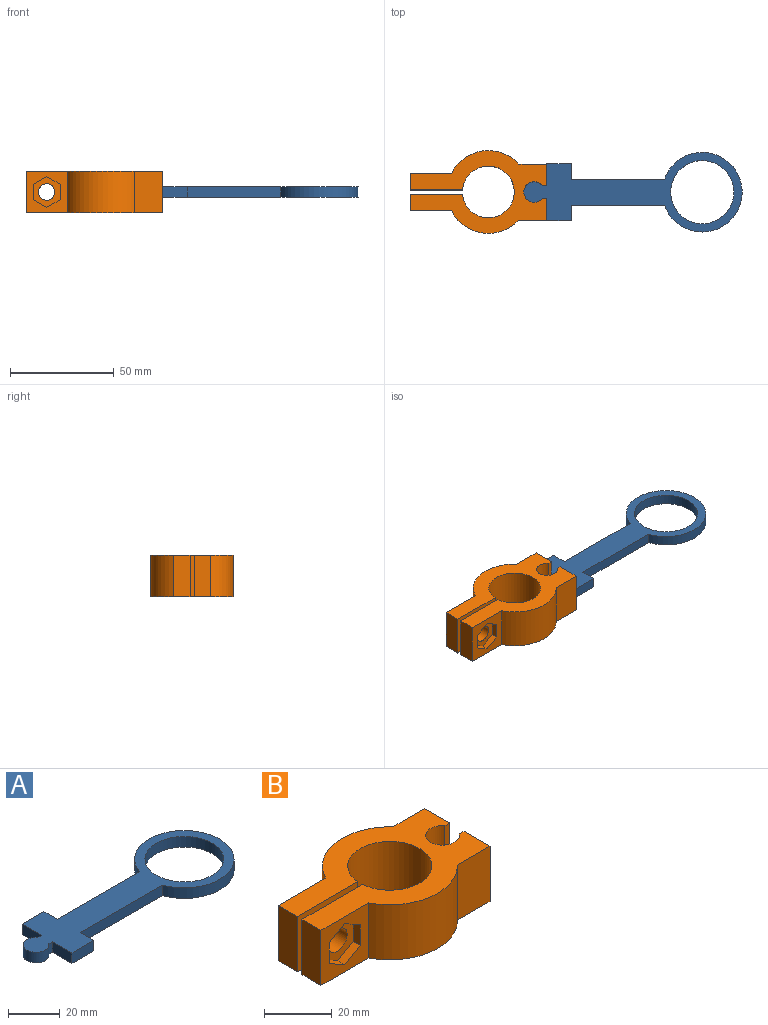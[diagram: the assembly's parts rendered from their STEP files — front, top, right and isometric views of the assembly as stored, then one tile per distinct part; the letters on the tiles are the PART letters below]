
ASSEMBLY  parts=2 mates=1
PART A: 15 faces, bbox 105.4x38.5x5 mm
  f0: plane 12x5mm, normal (0,-1,0), area 60mm2, adj f1,f12,f13,f14
  f1: plane 7.39x5mm, normal (1,0,0), area 37mm2, adj f0,f2,f13,f14
  f2: plane 44.99x5mm, normal (0,-1,0), area 224.9mm2, adj f1,f3,f13,f14
  f3: cylinder r=19.25mm len=38.5mm, axis (0,0,-1), area 540.7mm2, adj f2,f4,f13,f14
  f4: plane 44.99x5mm, normal (0,1,0), area 224.9mm2, adj f3,f5,f13,f14
  f5: plane 7.39x5mm, normal (1,0,0), area 37mm2, adj f4,f6,f13,f14
  f6: plane 12x5mm, normal (0,1,0), area 60mm2, adj f5,f7,f13,f14
  f7: plane 10.68x5mm, normal (-1,0,0), area 53.4mm2, adj f6,f8,f13,f14
  f8: plane 5x2mm, normal (0,1,0), area 10mm2, adj f7,f9,f13,f14
  f9: cylinder r=5mm len=10mm, axis (0,0,-1), area 124.9mm2, adj f8,f10,f13,f14
  f10: plane 5x2mm, normal (0,-1,0), area 10mm2, adj f9,f12,f13,f14
  f11: cylinder r=15.25mm len=30.5mm, axis (0,0,-1), area 479.1mm2, adj f13,f14
  f12: plane 10.68x5mm, normal (-1,0,0), area 53.4mm2, adj f0,f10,f13,f14
  f13: plane 105.43x38.5mm, normal (0,0,1), area 1405mm2, adj f0,f1,f2,f3,f4,f5,f6,f7
  f14: plane 105.43x38.5mm, normal (0,0,-1), area 1405mm2, adj f0,f1,f2,f3,f4,f5,f6,f7
PART B: 27 faces, bbox 66x40x20 mm
  f0: plane 20x20mm, normal (0,-1,0), area 253.6mm2, adj f4,f5,f16,f17,f18,f19,f20,f21
  f1: plane 25.4x20mm, normal (0,-1,0), area 457.8mm2, adj f2,f15,f16,f17,f26
  f2: cylinder r=12.5mm len=25mm, axis (0,0,-1), area 1530.8mm2, adj f1,f3,f16,f17
  f3: plane 25.41x20mm, normal (0,1,0), area 457.9mm2, adj f2,f4,f16,f17,f25
  f4: plane 20x7.96mm, normal (-1,0,0), area 159.2mm2, adj f0,f3,f16,f17
  f5: cylinder r=20mm len=32.28mm, axis (0,0,-1), area 763.8mm2, adj f0,f6,f16,f17
  f6: plane 20x13.7mm, normal (0,-1,0), area 274mm2, adj f5,f7,f16,f17
  f7: plane 20x10.86mm, normal (1,0,0), area 217.2mm2, adj f6,f8,f16,f17
  f8: plane 20x2mm, normal (0,1,0), area 40mm2, adj f7,f9,f16,f17
  f9: cylinder r=5mm len=20mm, axis (0,0,-1), area 499.6mm2, adj f8,f10,f16,f17
  f10: plane 20x2mm, normal (0,-1,0), area 40mm2, adj f9,f11,f16,f17
  f11: plane 20x10.49mm, normal (1,0,0), area 209.9mm2, adj f10,f12,f16,f17
  f12: plane 20x13.35mm, normal (0,1,0), area 267.1mm2, adj f11,f13,f16,f17
  f13: cylinder r=20mm len=32.63mm, axis (0,0,-1), area 773.9mm2, adj f12,f14,f16,f17
  f14: plane 20x20mm, normal (0,1,0), area 349.7mm2, adj f13,f15,f16,f17,f26
  f15: plane 20x8.02mm, normal (-1,0,0), area 160.5mm2, adj f1,f14,f16,f17
  f16: plane 65.98x40mm, normal (0,0,1), area 1230.7mm2, adj f0,f1,f2,f3,f4,f5,f6,f7
  f17: plane 65.98x40mm, normal (0,0,-1), area 1230.7mm2, adj f0,f1,f2,f3,f4,f5,f6,f7
  f18: plane 6.5x3.75mm, normal (-0.5,0,0.87), area 22.5mm2, adj f0,f19,f23,f24
  f19: plane 7.51x3mm, normal (-1,0,0), area 22.5mm2, adj f0,f18,f20,f24
  f20: plane 6.5x3.75mm, normal (-0.5,0,-0.87), area 22.5mm2, adj f0,f19,f21,f24
  f21: plane 6.5x3.75mm, normal (0.5,0,-0.87), area 22.5mm2, adj f0,f20,f22,f24
  f22: plane 7.51x3mm, normal (1,0,0), area 22.5mm2, adj f0,f21,f23,f24
  f23: plane 6.5x3.75mm, normal (0.5,0,0.87), area 22.5mm2, adj f0,f18,f22,f24
  f24: plane 15.01x13mm, normal (0,-1,0), area 96.1mm2, adj f18,f19,f20,f21,f22,f23,f25
  f25: cylinder r=4mm len=8mm, axis (0,-1,0), area 124.7mm2, adj f3,f24
  f26: cylinder r=4mm len=8.02mm, axis (0,-1,0), area 201.7mm2, adj f1,f14
PLACE A t=(108.18,77.87,23.11)mm
PLACE B t=(39.68,77.96,15.61)mm
MATE parallel B.f7 <-> A.f12  axis (1,0,0) through (67.79,69.53,25.61)mm
